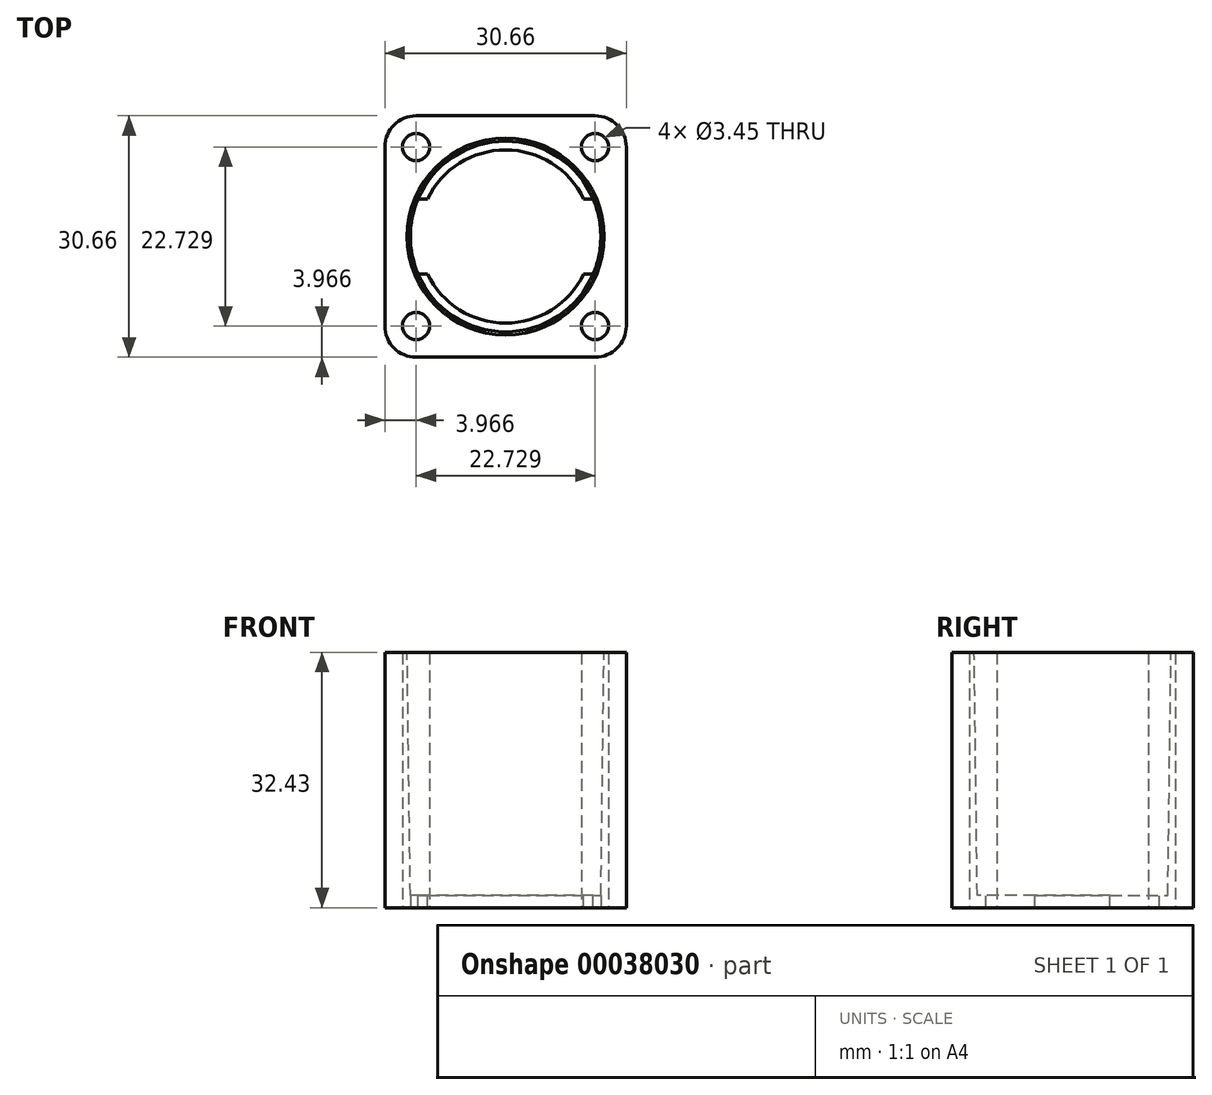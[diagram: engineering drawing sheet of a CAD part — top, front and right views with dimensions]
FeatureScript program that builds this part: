
annotation { "Feature Type Name" : "Feature", "Feature Type Description" : "" }
export const myFeature = defineFeature(function(context is Context, id is Id, definition is map)
    precondition{}
    {
        {
            var Q0;
            Q0=qCreatedBy(makeId("Top.planeOp"),FACE);
            var sketch = newSketch(context, id + "F0", { "sketchPlane" : qUnion([Q0])});
            skCircle(sketch, "E0", {"center": v(0, 0) * mm, "radius": 12.1 * mm});
            skLineSegment(sketch, "E1.rect.bottom", {"start": v(15.33, -15.33) * mm, "end": v(-15.33, -15.33) * mm});
            skLineSegment(sketch, "E1.rect.top", {"start": v(15.33, 15.33) * mm, "end": v(-15.33, 15.33) * mm});
            skLineSegment(sketch, "E1.rect.left", {"start": v(15.33, -15.33) * mm, "end": v(15.33, 15.33) * mm});
            skLineSegment(sketch, "E1.rect.right", {"start": v(-15.33, -15.33) * mm, "end": v(-15.33, 15.33) * mm});
            skCircle(sketch, "E2", {"center": v(11.36, -11.36) * mm, "radius": 1.73 * mm});
            skCircle(sketch, "E3", {"center": v(11.36, 11.36) * mm, "radius": 1.73 * mm});
            skCircle(sketch, "E4", {"center": v(-11.36, 11.36) * mm, "radius": 1.73 * mm});
            skCircle(sketch, "E5", {"center": v(-11.36, -11.36) * mm, "radius": 1.73 * mm});
            skLineSegment(sketch, "E6.rect.bottom", {"start": v(11.36, 11.36) * mm, "end": v(-11.36, 11.36) * mm, "construction": true});
            skLineSegment(sketch, "E6.rect.top", {"start": v(11.36, -11.36) * mm, "end": v(-11.36, -11.36) * mm, "construction": true});
            skLineSegment(sketch, "E6.rect.left", {"start": v(11.36, 11.36) * mm, "end": v(11.36, -11.36) * mm, "construction": true});
            skLineSegment(sketch, "E6.rect.right", {"start": v(-11.36, 11.36) * mm, "end": v(-11.36, -11.36) * mm, "construction": true});
            skCircle(sketch, "E7", {"center": v(-11.36, 11.36) * mm, "radius": 3.97 * mm, "construction": true});
            skSolve(sketch);
        }
        {
            var Q0;
            Q0=qSketchRegion(id+"F0",true);
            extrude(context, id + "F1", {"entities" : qUnion([Q0]), "depth" : 30.84 * mm});
        }
        {
            var Q0;
            Q0=makeQuery(id+"F1.opExtrude","CAP_FACE",FACE,{"disambiguationData":[OSD([sQuery(id+"F0.wireOp",EDGE,"E0"),sQuery(id+"F0.wireOp",EDGE,"E1.rect.bottom"),sQuery(id+"F0.wireOp",EDGE,"E1.rect.top"),sQuery(id+"F0.wireOp",EDGE,"E1.rect.left"),sQuery(id+"F0.wireOp",EDGE,"E1.rect.right"),sQuery(id+"F0.wireOp",EDGE,"E2"),sQuery(id+"F0.wireOp",EDGE,"E3"),sQuery(id+"F0.wireOp",EDGE,"E4"),sQuery(id+"F0.wireOp",EDGE,"E5")])],"isStart":true});
            var sketch = newSketch(context, id + "F2", { "sketchPlane" : qUnion([Q0])});
            skLineSegment(sketch, "E8.rect.bottom", {"start": v(15.33, 15.33) * mm, "end": v(-15.33, 15.33) * mm});
            skLineSegment(sketch, "E8.rect.top", {"start": v(15.33, -15.33) * mm, "end": v(-15.33, -15.33) * mm});
            skLineSegment(sketch, "E8.rect.left", {"start": v(15.33, 15.33) * mm, "end": v(15.33, -15.33) * mm});
            skLineSegment(sketch, "E8.rect.right", {"start": v(-15.33, 15.33) * mm, "end": v(-15.33, -15.33) * mm});
            skPoint(sketch, "E8.rect.middle", {"position": v(0, 0) * mm});
            skCircle(sketch, "E9", {"center": v(0, 0) * mm, "radius": 11 * mm});
            skSolve(sketch);
        }
        {
            var Q0;
            Q0=makeQuery(id+"F2.imprint","IMPRINT",FACE,{"disambiguationData":[TD([[makeQuery(id+"F2.imprint","IMPRINT",EDGE,{"derivedFrom":sQuery(id+"F2.wireOp",EDGE,"E9")}),-1.0]])]});
            var Q1;
            Q1=makeQuery(id+"F2.imprint","IMPRINT",FACE,{"disambiguationData":[TD([[makeQuery(id+"F2.imprint","IMPRINT",EDGE,{"derivedFrom":sQuery(id+"F2.wireOp",EDGE,"E8.rect.bottom")}),1.0]])]});
            extrude(context, id + "F3", {"entities" : qUnion([Q0, Q1]), "operationType" : NewBodyOperationType.ADD, "depth" : 1.59 * mm});
        }
        {
            var Q0;
            Q0=makeQuery(id+"F3.boolean.opBoolean","MERGE",EDGE,{"derivedFrom":[makeQuery(id+"F1.opExtrude","SWEPT_EDGE",EDGE,{"disambiguationData":[OSD([sQuery(id+"F0.wireOp",EDGE,"E1.rect.top"),sQuery(id+"F0.wireOp",EDGE,"E1.rect.right")])]}),makeQuery(id+"F3.opExtrude","SWEPT_EDGE",EDGE,{"disambiguationData":[OSD([sQuery(id+"F2.wireOp",EDGE,"E8.rect.top"),sQuery(id+"F2.wireOp",EDGE,"E8.rect.right")])]})]});
            var Q1;
            Q1=makeQuery(id+"F3.boolean.opBoolean","MERGE",EDGE,{"derivedFrom":[makeQuery(id+"F1.opExtrude","SWEPT_EDGE",EDGE,{"disambiguationData":[OSD([sQuery(id+"F0.wireOp",EDGE,"E1.rect.top"),sQuery(id+"F0.wireOp",EDGE,"E1.rect.left")])]}),makeQuery(id+"F3.opExtrude","SWEPT_EDGE",EDGE,{"disambiguationData":[OSD([sQuery(id+"F2.wireOp",EDGE,"E8.rect.top"),sQuery(id+"F2.wireOp",EDGE,"E8.rect.left")])]})]});
            var Q2;
            Q2=makeQuery(id+"F3.boolean.opBoolean","MERGE",EDGE,{"derivedFrom":[makeQuery(id+"F1.opExtrude","SWEPT_EDGE",EDGE,{"disambiguationData":[OSD([sQuery(id+"F0.wireOp",EDGE,"E1.rect.bottom"),sQuery(id+"F0.wireOp",EDGE,"E1.rect.left")])]}),makeQuery(id+"F3.opExtrude","SWEPT_EDGE",EDGE,{"disambiguationData":[OSD([sQuery(id+"F2.wireOp",EDGE,"E8.rect.bottom"),sQuery(id+"F2.wireOp",EDGE,"E8.rect.left")])]})]});
            var Q3;
            Q3=makeQuery(id+"F3.boolean.opBoolean","MERGE",EDGE,{"derivedFrom":[makeQuery(id+"F1.opExtrude","SWEPT_EDGE",EDGE,{"disambiguationData":[OSD([sQuery(id+"F0.wireOp",EDGE,"E1.rect.bottom"),sQuery(id+"F0.wireOp",EDGE,"E1.rect.right")])]}),makeQuery(id+"F3.opExtrude","SWEPT_EDGE",EDGE,{"disambiguationData":[OSD([sQuery(id+"F2.wireOp",EDGE,"E8.rect.bottom"),sQuery(id+"F2.wireOp",EDGE,"E8.rect.right")])]})]});
            fillet(context, id + "F4", {"entities" : qUnion([Q0, Q1, Q2, Q3]), "radius" : 3.97 * mm, "tangentPropagation" : true, "allowEdgeOverflow" : false});
        }
        {
            var Q0;
            Q0=makeQuery(id+"F3.opExtrude","CAP_FACE",FACE,{"disambiguationData":[OSD([sQuery(id+"F0.wireOp",EDGE,"E2"),sQuery(id+"F0.wireOp",EDGE,"E3"),sQuery(id+"F0.wireOp",EDGE,"E4"),sQuery(id+"F0.wireOp",EDGE,"E5"),sQuery(id+"F2.wireOp",EDGE,"E8.rect.bottom"),sQuery(id+"F2.wireOp",EDGE,"E8.rect.top"),sQuery(id+"F2.wireOp",EDGE,"E8.rect.left"),sQuery(id+"F2.wireOp",EDGE,"E8.rect.right"),sQuery(id+"F2.wireOp",EDGE,"E9")])],"isStart":true});
            var sketch = newSketch(context, id + "F5", { "sketchPlane" : qUnion([Q0])});
            skArc(sketch, "E10", {"start": v(-9.92, 4.76) * mm, "mid": v(-11, 0) * mm, "end": v(-9.92, -4.76) * mm});
            skArc(sketch, "E11", {"start": v(-11.13, 4.76) * mm, "mid": v(-12.1, 0) * mm, "end": v(-11.13, -4.76) * mm});
            skArc(sketch, "E12", {"start": v(9.92, -4.76) * mm, "mid": v(11, 0) * mm, "end": v(9.92, 4.76) * mm});
            skArc(sketch, "E13", {"start": v(11.13, -4.76) * mm, "mid": v(12.1, 0) * mm, "end": v(11.13, 4.76) * mm});
            skLineSegment(sketch, "E14", {"start": v(-11.13, -4.76) * mm, "end": v(-9.92, -4.76) * mm});
            skLineSegment(sketch, "E15", {"start": v(-11.13, 4.76) * mm, "end": v(-9.92, 4.76) * mm});
            skLineSegment(sketch, "E16", {"start": v(11.13, 4.76) * mm, "end": v(9.92, 4.76) * mm});
            skLineSegment(sketch, "E17", {"start": v(9.92, -4.76) * mm, "end": v(11.13, -4.76) * mm});
            skLineSegment(sketch, "E18", {"start": v(-11, 0) * mm, "end": v(11, 0) * mm});
            skSolve(sketch);
        }
        {
            var Q0;
            Q0=qSketchRegion(id+"F5",true);
            extrude(context, id + "F6", {"entities" : qUnion([Q0]), "operationType" : NewBodyOperationType.REMOVE, "oppositeDirection" : true, "depth" : 25.4 * mm});
        }
        {
            var Q0;
            Q0=makeQuery(id+"F1.opExtrude","CAP_EDGE",EDGE,{"disambiguationData":[OSD([sQuery(id+"F0.wireOp",EDGE,"E0")])],"isStart":false});
            chamfer(context, id + "F7", {"entities" : qUnion([Q0]), "chamferType" : ChamferType.TWO_OFFSETS, "width1" : 30.84 * mm, "oppositeDirection" : false, "width2" : 0.4 * mm, "tangentPropagation" : true});
        }
    });
